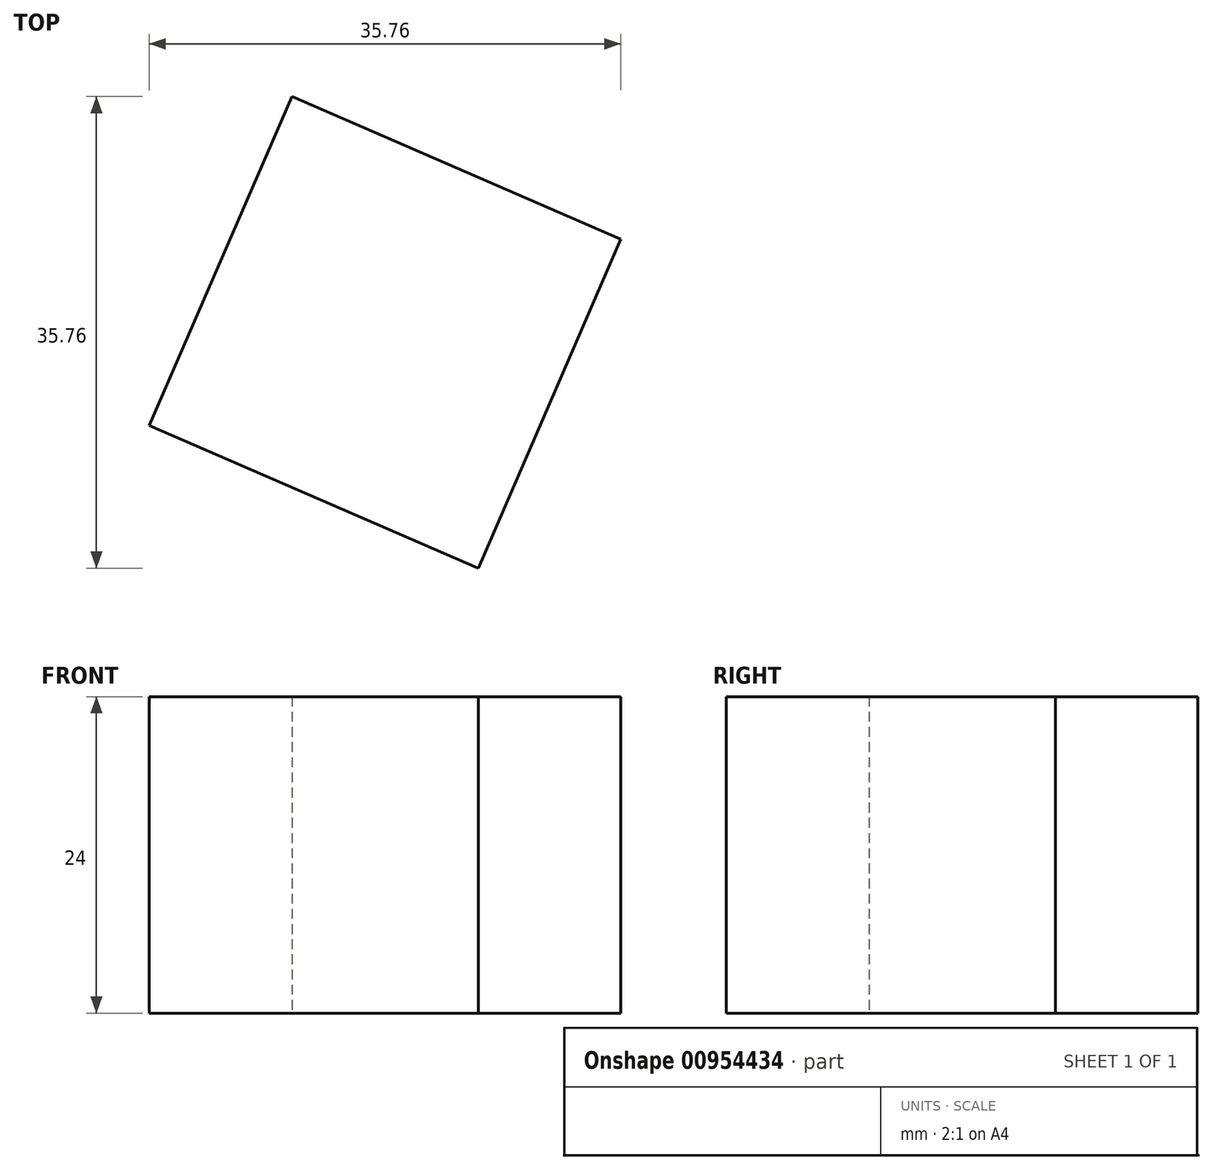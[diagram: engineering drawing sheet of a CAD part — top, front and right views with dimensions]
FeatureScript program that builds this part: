
annotation { "Feature Type Name" : "Feature", "Feature Type Description" : "" }
export const myFeature = defineFeature(function(context is Context, id is Id, definition is map)
    precondition{}
    {
        {
            var Q0;
            Q0=qCreatedBy(makeId("Top.planeOp"),FACE);
            var sketch = newSketch(context, id + "F0", { "sketchPlane" : qUnion([Q0])});
            skCircle(sketch, "E0.cCircle", {"center": v(0, 0) * mm, "radius": 13.6 * mm, "construction": true});
            skLineSegment(sketch, "E0.0", {"start": v(17.88, 7.06) * mm, "end": v(7.06, -17.88) * mm});
            skLineSegment(sketch, "E0.1", {"start": v(7.06, -17.88) * mm, "end": v(-17.88, -7.06) * mm});
            skLineSegment(sketch, "E0.2", {"start": v(-17.88, -7.06) * mm, "end": v(-7.06, 17.88) * mm});
            skLineSegment(sketch, "E0.3", {"start": v(-7.06, 17.88) * mm, "end": v(17.88, 7.06) * mm});
            skPoint(sketch, "E0.0.midPoint", {"position": v(12.47, -5.4) * mm});
            skSolve(sketch);
        }
        {
            var Q0;
            Q0=makeQuery(id+"F0.imprint","IMPRINT",FACE,{"disambiguationData":[TD([[makeQuery(id+"F0.imprint","IMPRINT",EDGE,{"derivedFrom":sQuery(id+"F0.wireOp",EDGE,"E0.0")}),-1.0]])]});
            extrude(context, id + "F1", {"entities" : qUnion([Q0]), "depth" : 24 * mm, "offsetDistance" : 25 * mm});
        }
    });
